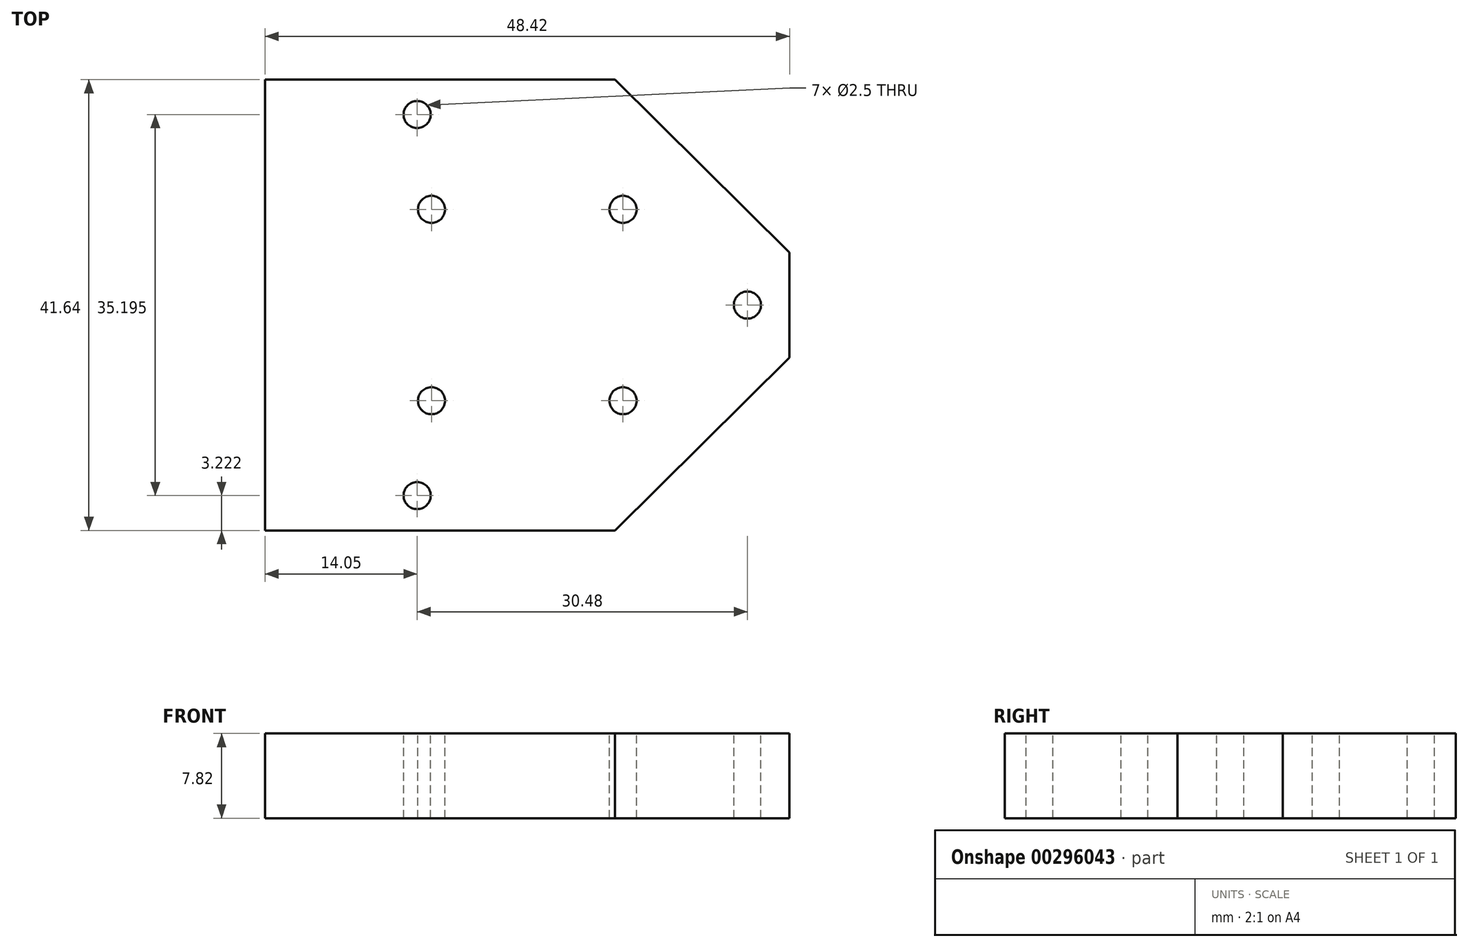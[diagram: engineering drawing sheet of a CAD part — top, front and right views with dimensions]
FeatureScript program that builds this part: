
annotation { "Feature Type Name" : "Feature", "Feature Type Description" : "" }
export const myFeature = defineFeature(function(context is Context, id is Id, definition is map)
    precondition{}
    {
        {
            var Q0;
            Q0=qCreatedBy(makeId("Top.planeOp"),FACE);
            var sketch = newSketch(context, id + "F0", { "sketchPlane" : qUnion([Q0])});
            skLineSegment(sketch, "E0", {"start": v(-24.2, -20.82) * mm, "end": v(8.1, -20.82) * mm});
            skLineSegment(sketch, "E1", {"start": v(-24.2, -20.82) * mm, "end": v(-24.2, 20.82) * mm});
            skLineSegment(sketch, "E2", {"start": v(-24.2, 20.82) * mm, "end": v(-24.2, 0) * mm});
            skLineSegment(sketch, "E3", {"start": v(-24.2, 0) * mm, "end": v(0, 0) * mm, "construction": true});
            skPoint(sketch, "E4.endSnap0", {"position": v(-8.05, -20.82) * mm});
            skLineSegment(sketch, "E5", {"start": v(0, 0) * mm, "end": v(0, -20.82) * mm, "construction": true});
            skLineSegment(sketch, "E6", {"start": v(-24.2, 20.82) * mm, "end": v(8.1, 20.82) * mm});
            skLineSegment(sketch, "E7", {"start": v(0, 0) * mm, "end": v(24.2, 0) * mm, "construction": true});
            skLineSegment(sketch, "E8", {"start": v(24.2, 0) * mm, "end": v(24.2, 4.85) * mm, "construction": true});
            skLineSegment(sketch, "E9", {"start": v(24.2, 4.85) * mm, "end": v(24.2, 0) * mm});
            skLineSegment(sketch, "E10", {"start": v(24.2, 0) * mm, "end": v(24.2, -4.85) * mm});
            skLineSegment(sketch, "E11", {"start": v(24.2, 4.85) * mm, "end": v(8.1, 20.82) * mm});
            skLineSegment(sketch, "E12", {"start": v(24.2, -4.85) * mm, "end": v(8.1, -20.82) * mm});
            skSolve(sketch);
        }
        {
            var Q0;
            Q0 = qSketchRegion(id + "F0", true);
            extrude(context, id + "F1", {"entities" : qUnion([Q0]), "oppositeDirection" : true, "depth" : 7.82 * mm});
        }
        {
            var Q0;
            Q0=makeQuery(id+"F0.imprint","IMPRINT",FACE,{"disambiguationData":[TD([[makeQuery(id+"F0.imprint","IMPRINT",EDGE,{"derivedFrom":sQuery(id+"F0.wireOp",EDGE,"E0")}),1.0]])]});
            var sketch = newSketch(context, id + "F2", { "sketchPlane" : qUnion([Q0])});
            skCircle(sketch, "E13", {"center": v(0, 0) * mm, "radius": 12.5 * mm, "construction": true});
            skLineSegment(sketch, "E14", {"start": v(0, 0) * mm, "end": v(-8.84, 8.84) * mm, "construction": true});
            skLineSegment(sketch, "E15", {"start": v(0, 0) * mm, "end": v(-8.84, -8.84) * mm, "construction": true});
            skLineSegment(sketch, "E16", {"start": v(8.84, -8.84) * mm, "end": v(0, 0) * mm, "construction": true});
            skLineSegment(sketch, "E17", {"start": v(8.84, 8.84) * mm, "end": v(0, 0) * mm, "construction": true});
            skSolve(sketch);
        }
        {
            var Q0;
            Q0=makeQuery(id+"F0.imprint","IMPRINT",FACE,{"disambiguationData":[TD([[makeQuery(id+"F0.imprint","IMPRINT",EDGE,{"derivedFrom":sQuery(id+"F0.wireOp",EDGE,"E0")}),1.0]])]});
            var sketch = newSketch(context, id + "F3", { "sketchPlane" : qUnion([Q0])});
            skLineSegment(sketch, "E18", {"start": v(0, 0) * mm, "end": v(20.32, 0) * mm, "construction": true});
            skCircle(sketch, "E19", {"center": v(0, 0) * mm, "radius": 20.32 * mm, "construction": true});
            skLineSegment(sketch, "E20", {"start": v(0, 0) * mm, "end": v(-10.16, 17.6) * mm, "construction": true});
            skLineSegment(sketch, "E21", {"start": v(0, 0) * mm, "end": v(-10.16, -17.6) * mm, "construction": true});
            skCircle(sketch, "E22", {"center": v(-10.16, -17.6) * mm, "radius": 1.25 * mm});
            skCircle(sketch, "E23", {"center": v(-10.16, 17.6) * mm, "radius": 1.25 * mm});
            skCircle(sketch, "E24", {"center": v(20.32, 0) * mm, "radius": 1.25 * mm});
            skCircle(sketch, "E25", {"center": v(-8.84, -8.84) * mm, "radius": 1.25 * mm});
            skCircle(sketch, "E26", {"center": v(-8.84, 8.84) * mm, "radius": 1.25 * mm});
            skCircle(sketch, "E27", {"center": v(8.84, 8.84) * mm, "radius": 1.25 * mm});
            skCircle(sketch, "E28", {"center": v(8.84, -8.84) * mm, "radius": 1.25 * mm});
            skSolve(sketch);
        }
        {
            var Q0;
            Q0 = qSketchRegion(id + "F3", true);
            var Q1;
            Q1=makeQuery(id+"F1.opExtrude","CAP_FACE",FACE,{"disambiguationData":[OSD([sQuery(id+"F0.wireOp",EDGE,"E0"),sQuery(id+"F0.wireOp",EDGE,"E1"),sQuery(id+"F0.wireOp",EDGE,"E2"),sQuery(id+"F0.wireOp",EDGE,"E6"),sQuery(id+"F0.wireOp",EDGE,"E9"),sQuery(id+"F0.wireOp",EDGE,"E10"),sQuery(id+"F0.wireOp",EDGE,"E11"),sQuery(id+"F0.wireOp",EDGE,"E12")])],"isStart":false});
            extrude(context, id + "F4", {"entities" : qUnion([Q0]), "operationType" : NewBodyOperationType.REMOVE, "endBound" : BoundingType.UP_TO_SURFACE, "oppositeDirection" : true, "endBoundEntityFace" : qUnion([Q1]), "depth" : 10.16 * mm});
        }
    });
